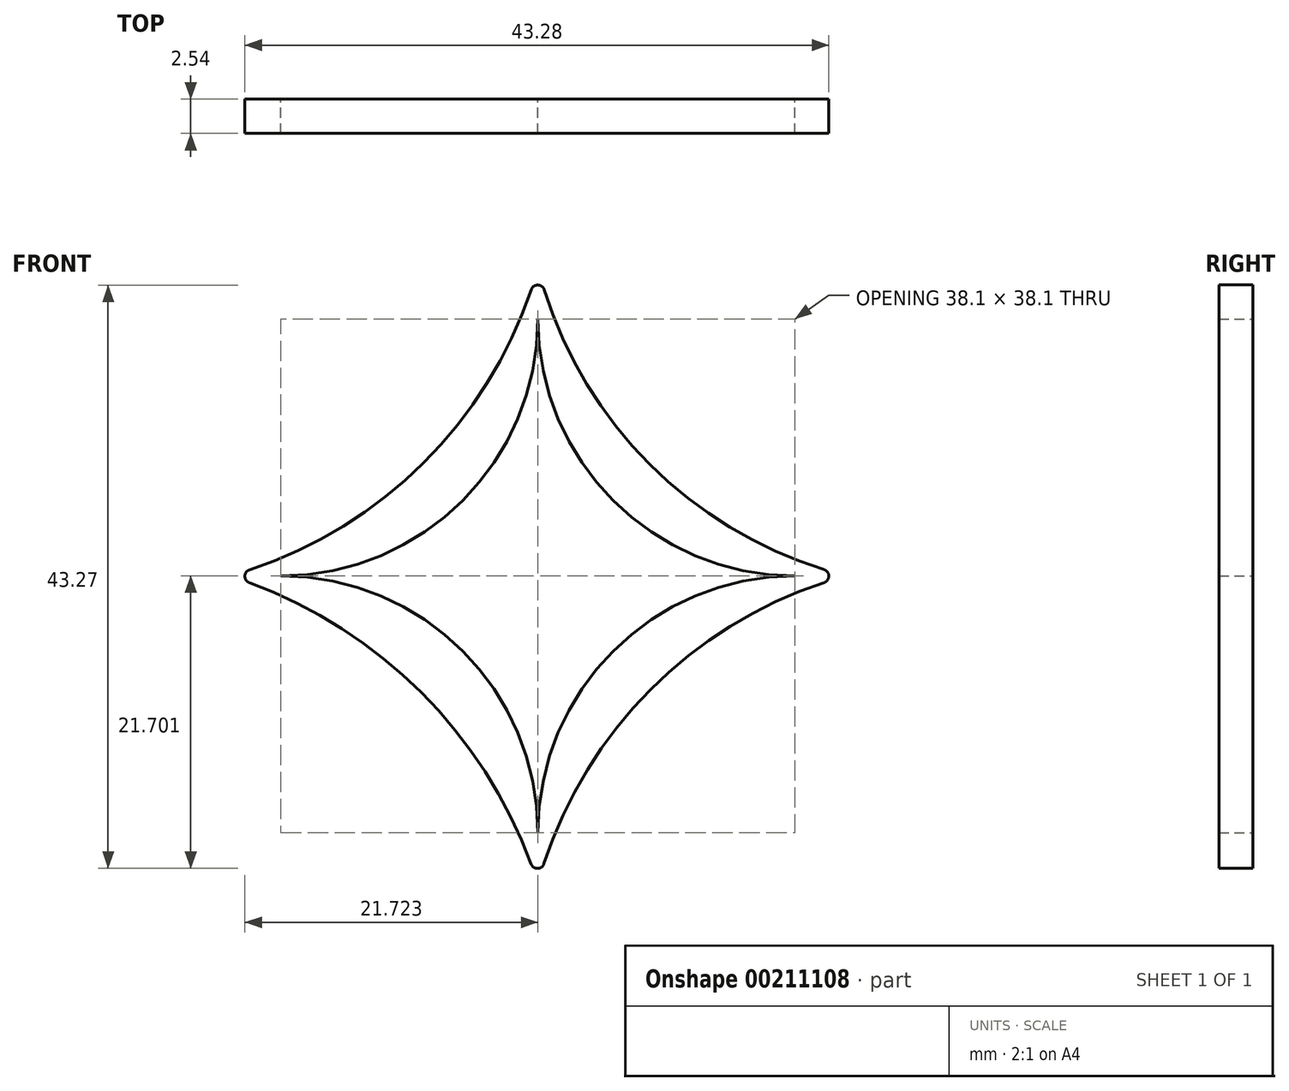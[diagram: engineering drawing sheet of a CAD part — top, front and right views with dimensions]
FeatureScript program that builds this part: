
annotation { "Feature Type Name" : "Feature", "Feature Type Description" : "" }
export const myFeature = defineFeature(function(context is Context, id is Id, definition is map)
    precondition{}
    {
        {
            var Q0;
            Q0=qCreatedBy(makeId("Front.planeOp"),FACE);
            var sketch = newSketch(context, id + "F0", { "sketchPlane" : qUnion([Q0])});
            skLineSegment(sketch, "E0", {"start": v(45.76, 0) * mm, "end": v(47.03, -3.94) * mm});
            skLineSegment(sketch, "E1", {"start": v(0.01, 1.37) * mm, "end": v(0.01, -17.68) * mm});
            skLineSegment(sketch, "E2", {"start": v(0.01, -17.68) * mm, "end": v(0.01, 1.37) * mm});
            skLineSegment(sketch, "E3", {"start": v(0.01, 1.37) * mm, "end": v(0.01, 20.42) * mm});
            skLineSegment(sketch, "E4", {"start": v(0.01, 1.37) * mm, "end": v(19.06, 1.37) * mm});
            skLineSegment(sketch, "E5", {"start": v(0.01, 1.37) * mm, "end": v(-19.04, 1.37) * mm});
            skArc(sketch, "E6", {"start": v(-19.04, 1.37) * mm, "mid": v(-5.57, 6.95) * mm, "end": v(0.01, 20.42) * mm});
            skArc(sketch, "E7", {"start": v(0.01, 20.42) * mm, "mid": v(5.6, 6.95) * mm, "end": v(19.06, 1.37) * mm});
            skArc(sketch, "E8", {"start": v(19.06, 1.37) * mm, "mid": v(5.6, -4.2) * mm, "end": v(0.01, -17.68) * mm});
            skArc(sketch, "E9", {"start": v(0.01, -17.68) * mm, "mid": v(-5.57, -4.2) * mm, "end": v(-19.04, 1.37) * mm});
            skLineSegment(sketch, "E10.0", {"start": v(22.87, -17.68) * mm, "end": v(22.87, 1.37) * mm});
            skLineSegment(sketch, "E11.0", {"start": v(0.01, -21.49) * mm, "end": v(19.06, -21.49) * mm});
            skLineSegment(sketch, "E12.0", {"start": v(0.01, 24.23) * mm, "end": v(-19.04, 24.23) * mm});
            skLineSegment(sketch, "E13.0", {"start": v(-22.85, -17.68) * mm, "end": v(-22.85, 1.37) * mm});
            skArc(sketch, "E14", {"start": v(-22.85, 1.37) * mm, "mid": v(-8.42, 9.8) * mm, "end": v(0.01, 24.23) * mm});
            skArc(sketch, "E15", {"start": v(0.01, 24.23) * mm, "mid": v(8.3, 9.65) * mm, "end": v(22.87, 1.37) * mm});
            skArc(sketch, "E16", {"start": v(22.87, 1.37) * mm, "mid": v(8.4, -7.02) * mm, "end": v(0.01, -21.49) * mm});
            skArc(sketch, "E17", {"start": v(0.01, -21.49) * mm, "mid": v(-8.64, -7.28) * mm, "end": v(-22.85, 1.37) * mm});
            skLineSegment(sketch, "E18.0", {"start": v(1.28, 1.37) * mm, "end": v(1.28, 20.42) * mm});
            skLineSegment(sketch, "E19.0", {"start": v(1.28, -17.68) * mm, "end": v(1.28, 1.37) * mm});
            skLineSegment(sketch, "E20.0", {"start": v(-1.26, -17.68) * mm, "end": v(-1.26, 1.37) * mm});
            skLineSegment(sketch, "E21.0", {"start": v(-1.26, 1.37) * mm, "end": v(-1.26, 20.42) * mm});
            skSolve(sketch);
        }
        {
            var Q0;
            {var subQ2=sQuery(id+"F0.wireOp",EDGE,"E14");Q0=makeQuery(id+"F0.imprint","IMPRINT",FACE,{"disambiguationData":[TD([[makeQuery(id+"F0.imprint","IMPRINT",EDGE,{"derivedFrom":subQ2}),-1.0]])]});}
            extrude(context, id + "F1", {"entities" : qUnion([Q0]), "depth" : 2.54 * mm});
        }
        {
            var Q0;
            Q0=makeQuery(id+"F1.opExtrude","SWEPT_EDGE",EDGE,{"disambiguationData":[OSD([sQuery(id+"F0.wireOp",EDGE,"E14"),sQuery(id+"F0.wireOp",EDGE,"E15")])]});
            var Q1;
            Q1=makeQuery(id+"F1.opExtrude","SWEPT_EDGE",EDGE,{"disambiguationData":[OSD([sQuery(id+"F0.wireOp",EDGE,"E15"),sQuery(id+"F0.wireOp",EDGE,"E16")])]});
            var Q2;
            Q2=makeQuery(id+"F1.opExtrude","SWEPT_EDGE",EDGE,{"disambiguationData":[OSD([sQuery(id+"F0.wireOp",EDGE,"E16"),sQuery(id+"F0.wireOp",EDGE,"E17")])]});
            var Q3;
            Q3=makeQuery(id+"F1.opExtrude","SWEPT_EDGE",EDGE,{"disambiguationData":[OSD([sQuery(id+"F0.wireOp",EDGE,"E14"),sQuery(id+"F0.wireOp",EDGE,"E17")])]});
            fillet(context, id + "F2", {"entities" : qUnion([Q0, Q1, Q2, Q3]), "radius" : 0.5 * mm, "tangentPropagation" : true, "allowEdgeOverflow" : false});
        }
    });
